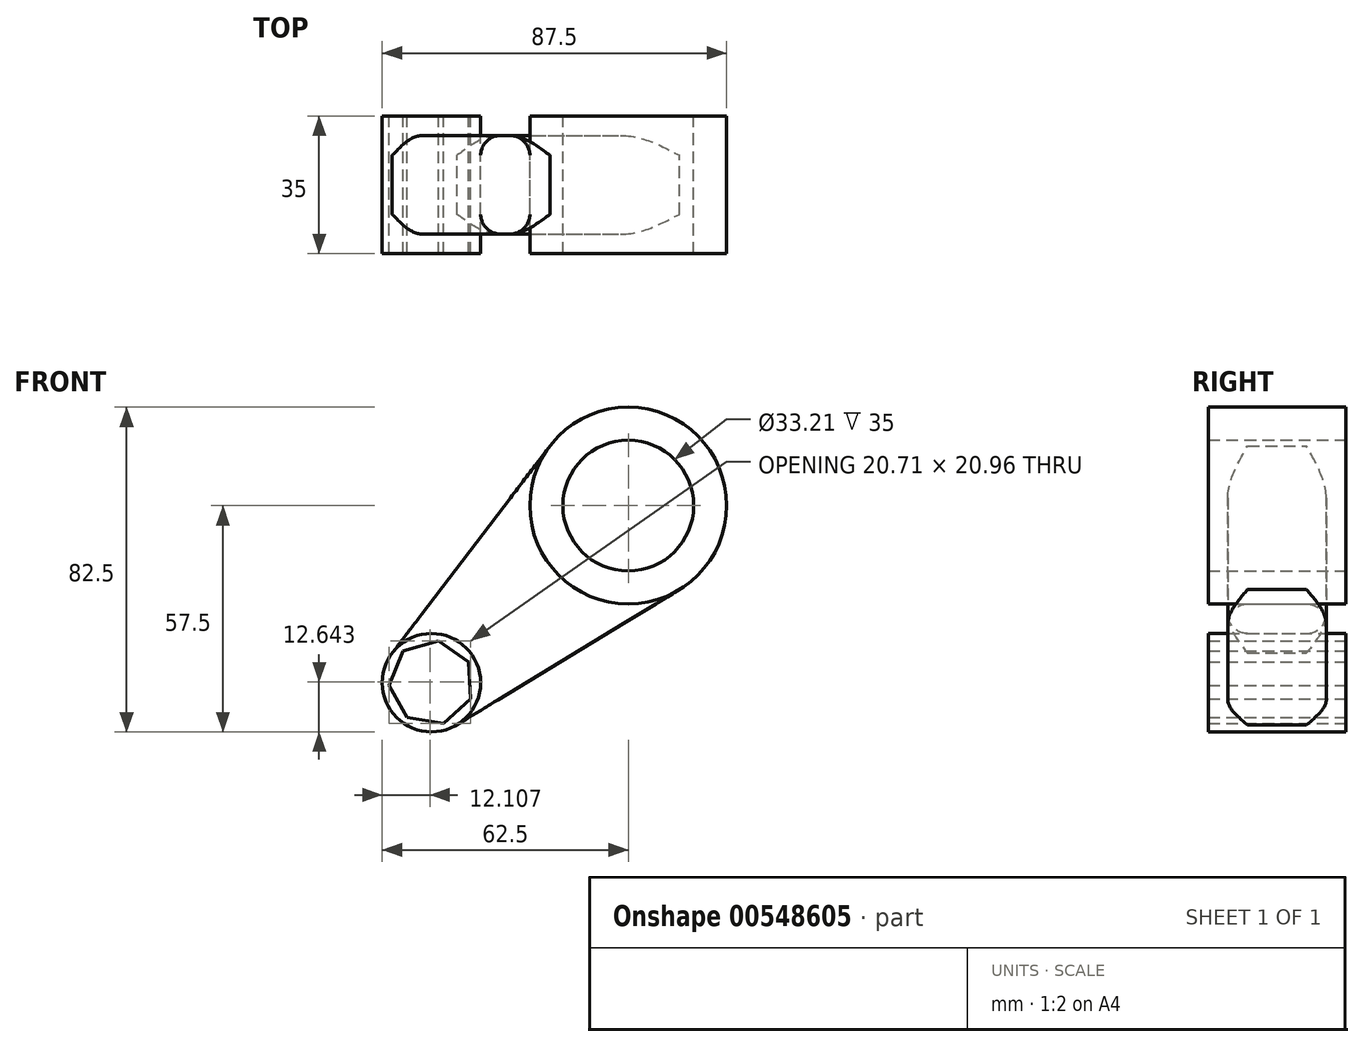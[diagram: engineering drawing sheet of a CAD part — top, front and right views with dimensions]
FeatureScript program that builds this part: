
annotation { "Feature Type Name" : "Feature", "Feature Type Description" : "" }
export const myFeature = defineFeature(function(context is Context, id is Id, definition is map)
    precondition{}
    {
        {
            var Q0;
            Q0=qCreatedBy(makeId("Front.planeOp"),FACE);
            var sketch = newSketch(context, id + "F0", { "sketchPlane" : qUnion([Q0])});
            skCircle(sketch, "E0", {"center": v(0, 0) * mm, "radius": 25 * mm});
            skCircle(sketch, "E1", {"center": v(-50, -45) * mm, "radius": 12.5 * mm});
            skLineSegment(sketch, "E2", {"start": v(-59.94, -37.42) * mm, "end": v(-19.89, 15.15) * mm});
            skLineSegment(sketch, "E3", {"start": v(0, 0) * mm, "end": v(-50, -45) * mm, "construction": true});
            skLineSegment(sketch, "E4.MirrorCS", {"start": v(-43.51, -55.68) * mm, "end": v(12.98, -21.37) * mm});
            skCircle(sketch, "E5", {"center": v(0, 0) * mm, "radius": 16.6 * mm});
            skCircle(sketch, "E6.cCircle", {"center": v(-50, -45) * mm, "radius": 9.7 * mm, "construction": true});
            skLineSegment(sketch, "E6.0", {"start": v(-40.04, -49.09) * mm, "end": v(-46.98, -55.34) * mm});
            skLineSegment(sketch, "E6.1", {"start": v(-46.98, -55.34) * mm, "end": v(-56.2, -53.8) * mm});
            skLineSegment(sketch, "E6.2", {"start": v(-56.2, -53.8) * mm, "end": v(-60.75, -45.64) * mm});
            skLineSegment(sketch, "E6.3", {"start": v(-60.75, -45.64) * mm, "end": v(-57.2, -37) * mm});
            skLineSegment(sketch, "E6.4", {"start": v(-57.2, -37) * mm, "end": v(-48.23, -34.38) * mm});
            skLineSegment(sketch, "E6.5", {"start": v(-48.23, -34.38) * mm, "end": v(-40.6, -39.76) * mm});
            skLineSegment(sketch, "E6.6", {"start": v(-40.6, -39.76) * mm, "end": v(-40.04, -49.09) * mm});
            skPoint(sketch, "E6.0.midPoint", {"position": v(-43.51, -52.21) * mm});
            skSolve(sketch);
        }
        {
            var Q0;
            Q0=makeQuery(id+"F0.imprint","IMPRINT",FACE,{"disambiguationData":[TD([[makeQuery(id+"F0.imprint","IMPRINT",EDGE,{"derivedFrom":sQuery(id+"F0.wireOp",EDGE,"E6.0")}),1.0]])]});
            var Q1;
            Q1=makeQuery(id+"F0.imprint","IMPRINT",FACE,{"disambiguationData":[TD([[makeQuery(id+"F0.imprint","IMPRINT",EDGE,{"derivedFrom":sQuery(id+"F0.wireOp",EDGE,"E5")}),-1.0]])]});
            extrude(context, id + "F1", {"entities" : qUnion([Q0, Q1]), "endBound" : BoundingType.SYMMETRIC, "depth" : 35 * mm, "offsetDistance" : 25 * mm});
        }
        {
            var Q0;
            {var subQ0=sQuery(id+"F0.wireOp",EDGE,"E2");Q0=makeQuery(id+"F0.imprint","IMPRINT",FACE,{"disambiguationData":[TD([[makeQuery(id+"F0.imprint","IMPRINT",EDGE,{"derivedFrom":subQ0}),-1.0]])]});}
            extrude(context, id + "F2", {"entities" : qUnion([Q0]), "endBound" : BoundingType.SYMMETRIC, "depth" : 25 * mm, "offsetDistance" : 25 * mm});
        }
        {
            var Q0;
            Q0=makeQuery(id+"F2.opExtrude","CAP_EDGE",EDGE,{"disambiguationData":[OSD([sQuery(id+"F0.wireOp",EDGE,"E0")])],"isStart":false});
            var Q1;
            Q1=makeQuery(id+"F2.opExtrude","CAP_EDGE",EDGE,{"disambiguationData":[OSD([sQuery(id+"F0.wireOp",EDGE,"E1")])],"isStart":false});
            var Q2;
            Q2=makeQuery(id+"F2.opExtrude","CAP_EDGE",EDGE,{"disambiguationData":[OSD([sQuery(id+"F0.wireOp",EDGE,"E1")])],"isStart":true});
            var Q3;
            Q3=makeQuery(id+"F2.opExtrude","CAP_EDGE",EDGE,{"disambiguationData":[OSD([sQuery(id+"F0.wireOp",EDGE,"E0")])],"isStart":true});
            fillet(context, id + "F3", {"entities" : qUnion([Q0, Q1, Q2, Q3]), "radius" : 5 * mm, "tangentPropagation" : true, "allowEdgeOverflow" : false});
        }
    });
